# Revit family: AD-S10T - M10 Eye Bolts
name_source: partatom
category: Communication Devices
revit_build: Autodesk Revit Architecture 2012 (Build: 20110309_2315(x64)
units: mm (PartAtom-declared; Revit-internal decimal feet)

## types (1)
- AD-S10T - M10 Eye Bolts
    100V Taps = 100, 50, 25
    70V Taps = 100, 50, 25, 12.5
    Coverage Horizontal = 90.00°
    Coverage Vertical = 90.00°
    Description = 10" 2-Way Surface Mount Loudspeaker
    Enclosure Finish = Black Finish
    Grille Finish = Black Grille
    Impedance = 8
    Manufacturer = QSC Audio Products, LLC
    Manufacturer URL = www.qscaudio.com
    Mid Depth = 286.0 mm
    Model = AD-S10T
    Power Handling = 250
    Product Documentation Link = TBA
    Product Page URL = TBA
    Regulatory Compliance = RoHS
    Rotation Axis Distance = 2491.3 mm
    SPL Max = 122
    Sensitivity = 92
    URL = TBA
    Weight Dimensional (kg) = 18.45
    Weight Dimensional (lb) = 40.6
    Weight Product (kg) = 15
    Weight Product (lb) = 31
    Width = 318.0 mm

## geometry (parser evidence)
native form markers: Blend x2, Sweep x3
no freeform markers — native parametric forms only
